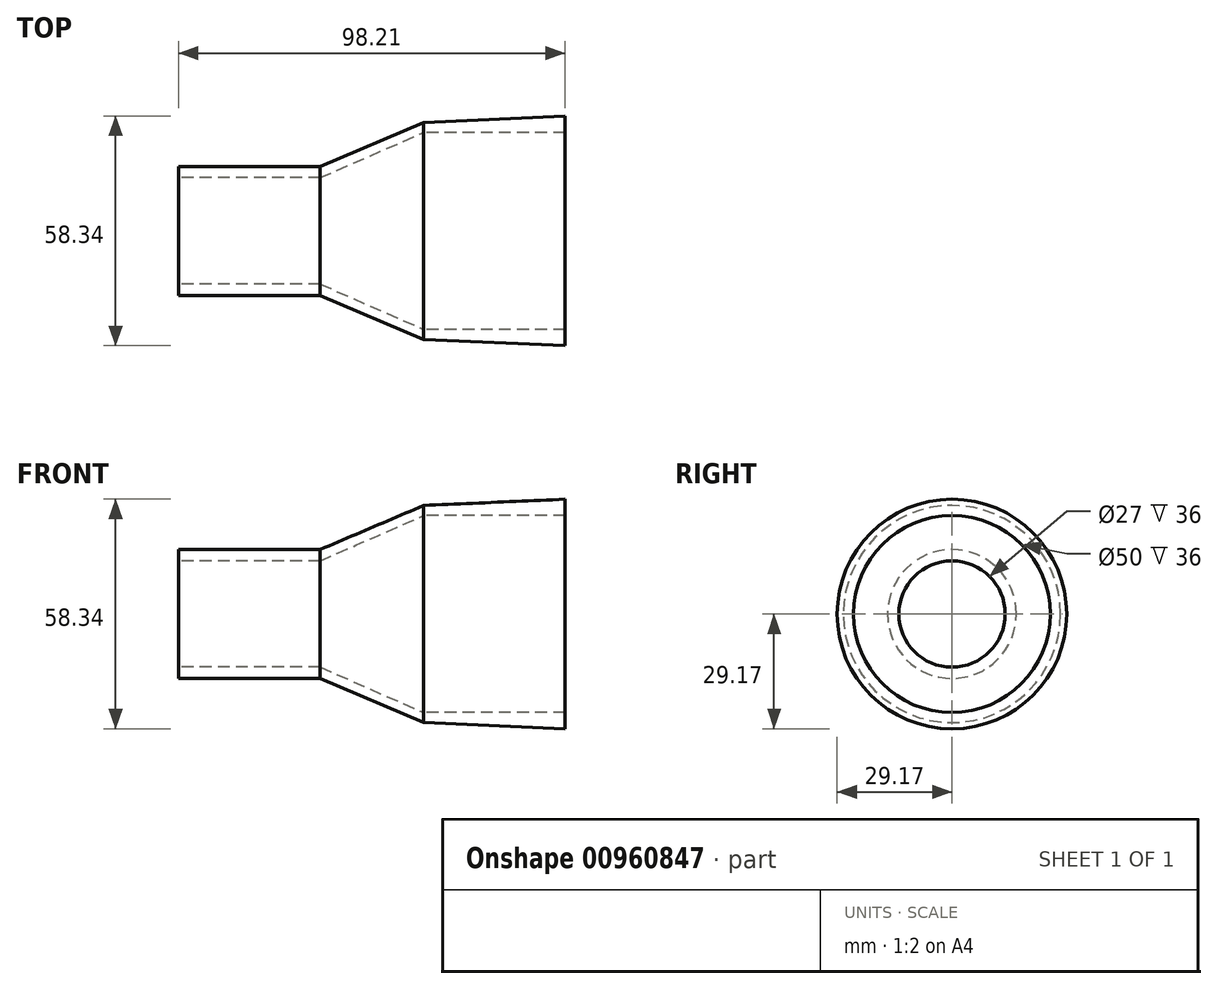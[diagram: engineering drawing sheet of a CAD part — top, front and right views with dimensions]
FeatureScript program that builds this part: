
annotation { "Feature Type Name" : "Feature", "Feature Type Description" : "" }
export const myFeature = defineFeature(function(context is Context, id is Id, definition is map)
    precondition{}
    {
        {
            var Q0;
            Q0=qCreatedBy(makeId("Top.planeOp"),FACE);
            var sketch = newSketch(context, id + "F0", { "sketchPlane" : qUnion([Q0])});
            skLineSegment(sketch, "E0", {"start": v(40.7, 29.24) * mm, "end": v(40.7, 25) * mm});
            skLineSegment(sketch, "E1", {"start": v(40.7, 25) * mm, "end": v(4.7, 25) * mm});
            skLineSegment(sketch, "E2", {"start": v(4.7, 25) * mm, "end": v(-21.5, 13.5) * mm});
            skLineSegment(sketch, "E3", {"start": v(-21.5, 13.5) * mm, "end": v(-57.5, 13.5) * mm});
            skLineSegment(sketch, "E4", {"start": v(-57.5, 13.5) * mm, "end": v(-57.5, 16.38) * mm});
            skLineSegment(sketch, "E5", {"start": v(-57.5, 16.38) * mm, "end": v(-21.5, 16.38) * mm});
            skLineSegment(sketch, "E6", {"start": v(-21.5, 16.38) * mm, "end": v(4.7, 27.58) * mm});
            skLineSegment(sketch, "E7", {"start": v(4.7, 27.58) * mm, "end": v(42.43, 29.24) * mm});
            skLineSegment(sketch, "E8", {"start": v(-43.34, 0) * mm, "end": v(39.1, 0) * mm, "construction": true});
            skLineSegment(sketch, "E9", {"start": v(22.7, 25) * mm, "end": v(22.7, 0) * mm, "construction": true});
            skPoint(sketch, "E10", {"position": v(-31.2, 13.5) * mm});
            skLineSegment(sketch, "E11", {"start": v(-31.2, 13.5) * mm, "end": v(-31.2, 0) * mm, "construction": true});
            skSolve(sketch);
        }
        {
            var Q0;
            {var subQ0=sQuery(id+"F0.wireOp",EDGE,"E1");Q0=makeQuery(id+"F0.imprint","IMPRINT",FACE,{"disambiguationData":[TD([[makeQuery(id+"F0.imprint","IMPRINT",EDGE,{"derivedFrom":subQ0}),-1.0]])]});}
            var Q1;
            Q1=sQuery(id+"F0.wireOp",EDGE,"E8");
            revolve(context, id + "F1", {"surfaceOperationType" : NewSurfaceOperationType.NEW, "entities" : qUnion([Q0]), "axis" : qUnion([Q1]), "revolveType" : RevolveType.FULL});
        }
    });
